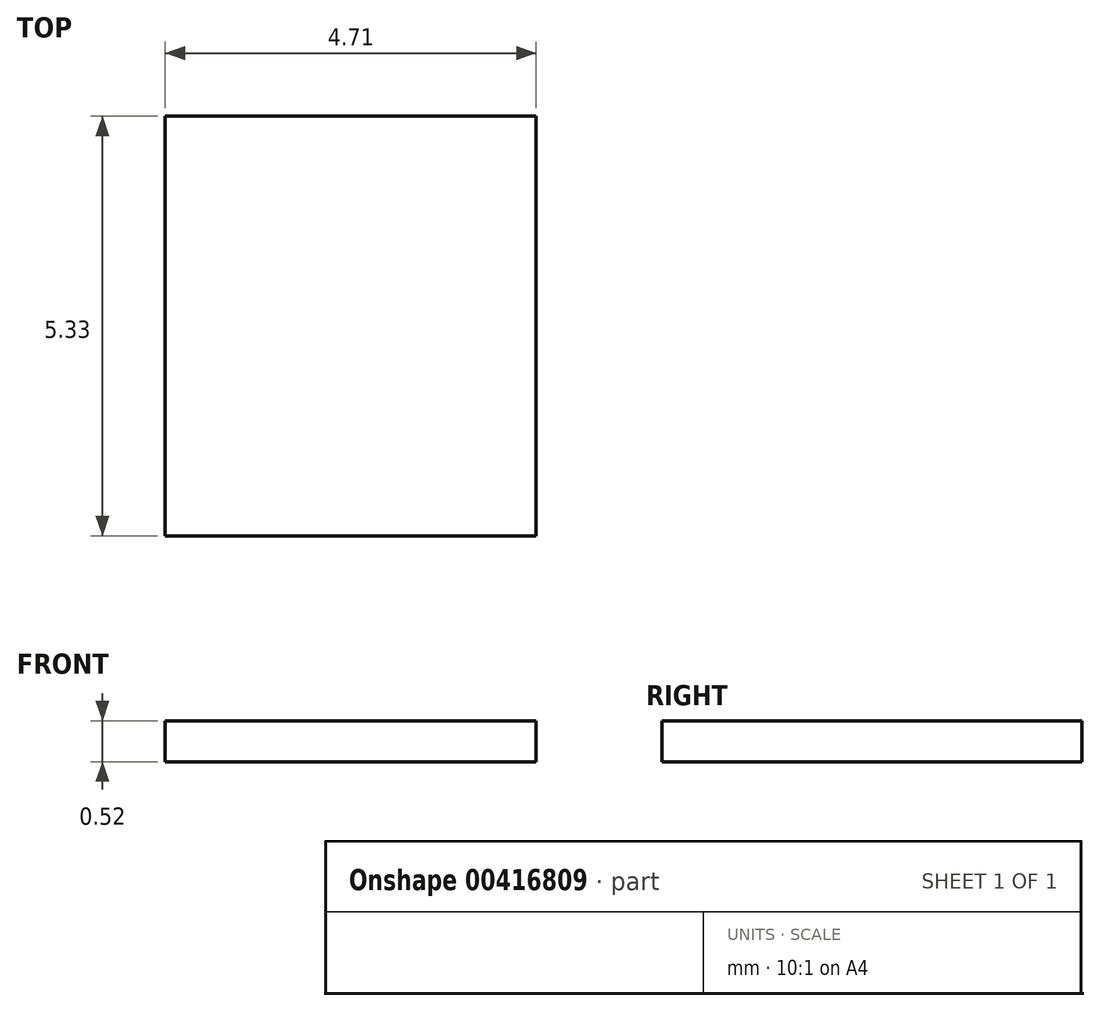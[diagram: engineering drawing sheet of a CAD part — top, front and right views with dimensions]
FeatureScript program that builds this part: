
annotation { "Feature Type Name" : "Feature", "Feature Type Description" : "" }
export const myFeature = defineFeature(function(context is Context, id is Id, definition is map)
    precondition{}
    {
        {
            var Q0;
            Q0=qCreatedBy(makeId("Top.planeOp"),FACE);
            var sketch = newSketch(context, id + "F0", { "sketchPlane" : qUnion([Q0])});
            skLineSegment(sketch, "E0.bottom", {"start": v(0, 0) * mm, "end": v(4.7, 0) * mm});
            skLineSegment(sketch, "E0.top", {"start": v(0, 5.33) * mm, "end": v(4.7, 5.33) * mm});
            skLineSegment(sketch, "E0.left", {"start": v(0, 0) * mm, "end": v(0, 5.33) * mm});
            skLineSegment(sketch, "E0.right", {"start": v(4.7, 0) * mm, "end": v(4.7, 5.33) * mm});
            skSolve(sketch);
        }
        {
            var Q0;
            Q0 = qSketchRegion(id + "F0", true);
            extrude(context, id + "F1", {"entities" : qUnion([Q0]), "depth" : .52 * mm, "offsetDistance" : 25.4 * mm});
        }
    });
